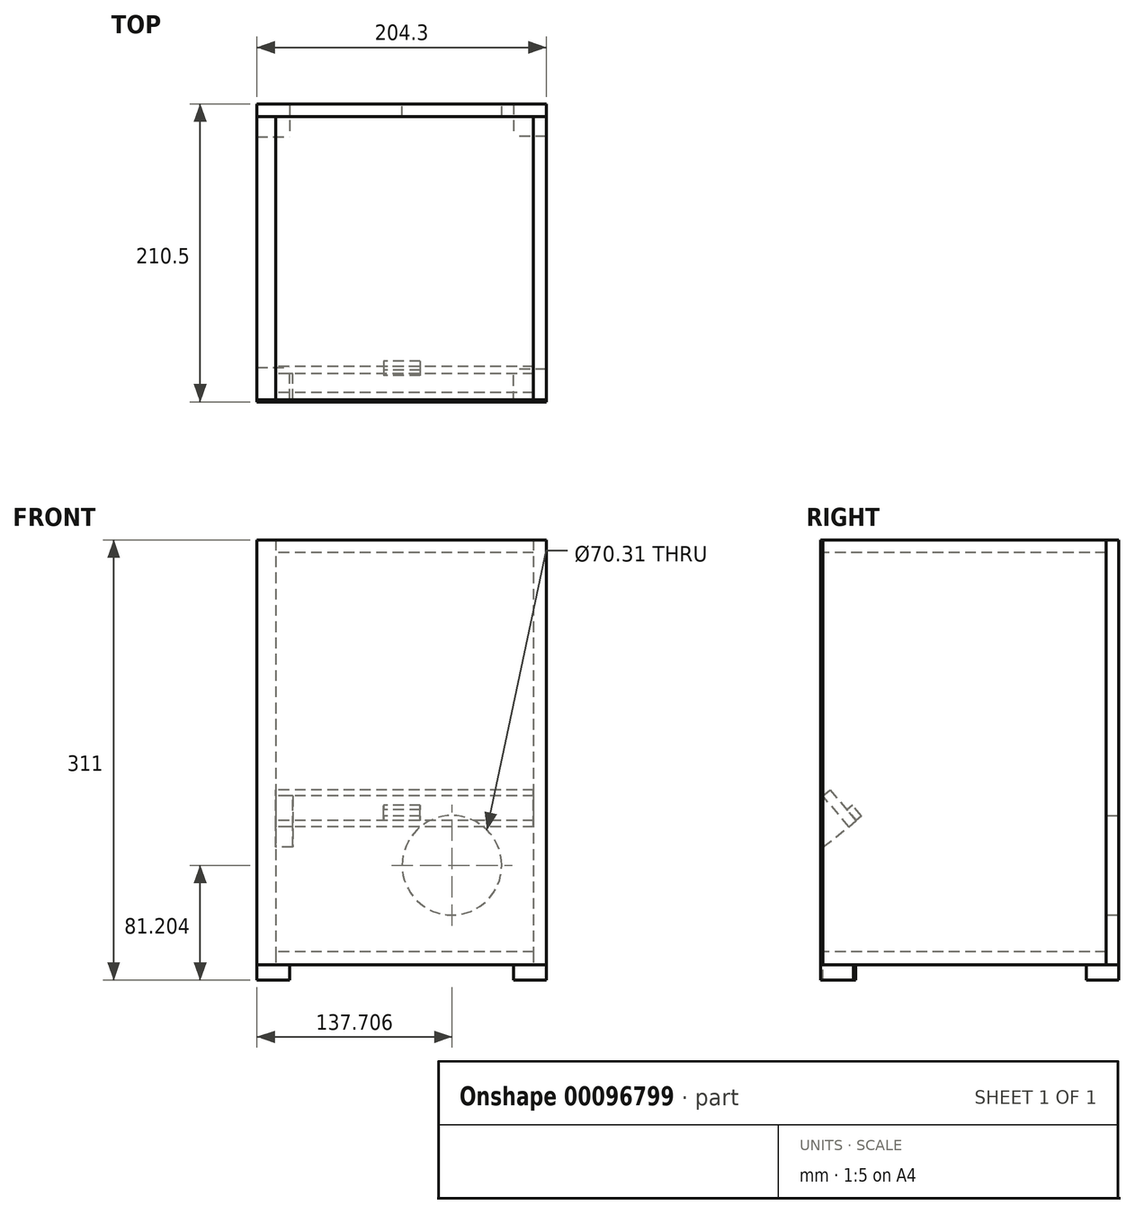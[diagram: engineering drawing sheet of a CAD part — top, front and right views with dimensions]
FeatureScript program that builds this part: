
annotation { "Feature Type Name" : "Feature", "Feature Type Description" : "" }
export const myFeature = defineFeature(function(context is Context, id is Id, definition is map)
    precondition{}
    {
        {
            var Q0;
            Q0=qCreatedBy(makeId("Front.planeOp"),FACE);
            var sketch = newSketch(context, id + "F0", { "sketchPlane" : qUnion([Q0])});
            skLineSegment(sketch, "E0.bottom", {"start": v(0, 0) * mm, "end": v(204.3, 0) * mm});
            skLineSegment(sketch, "E0.top", {"start": v(0, 300) * mm, "end": v(204.3, 300) * mm});
            skLineSegment(sketch, "E0.left", {"start": v(0, 0) * mm, "end": v(0, 300) * mm});
            skLineSegment(sketch, "E0.right", {"start": v(204.3, 0) * mm, "end": v(204.3, 300) * mm});
            skSolve(sketch);
        }
        {
            var Q0;
            Q0=makeQuery(id+"F0.imprint","IMPRINT",FACE,{"disambiguationData":[TD([[makeQuery(id+"F0.imprint","IMPRINT",EDGE,{"derivedFrom":sQuery(id+"F0.wireOp",EDGE,"E0.bottom")}),1.0]])]});
            extrude(context, id + "F1", {"entities" : qUnion([Q0]), "depth" : 1.5 * mm});
        }
        {
            var Q0;
            Q0=makeQuery(id+"F1.opExtrude","CAP_FACE",FACE,{"disambiguationData":[OSD([sQuery(id+"F0.wireOp",EDGE,"E0.bottom"),sQuery(id+"F0.wireOp",EDGE,"E0.top"),sQuery(id+"F0.wireOp",EDGE,"E0.left"),sQuery(id+"F0.wireOp",EDGE,"E0.right")])],"isStart":true});
            var sketch = newSketch(context, id + "F2", { "sketchPlane" : qUnion([Q0])});
            skLineSegment(sketch, "E1.bottom", {"start": v(0, 300) * mm, "end": v(-13.3, 300) * mm});
            skLineSegment(sketch, "E1.top", {"start": v(0, 0) * mm, "end": v(-13.3, 0) * mm});
            skLineSegment(sketch, "E1.left", {"start": v(0, 300) * mm, "end": v(0, 0) * mm});
            skLineSegment(sketch, "E1.right", {"start": v(-13.3, 300) * mm, "end": v(-13.3, 0) * mm});
            skSolve(sketch);
        }
        {
            var Q0;
            Q0 = qSketchRegion(id + "F2", true);
            extrude(context, id + "F3", {"entities" : qUnion([Q0]), "depth" : 200 * mm});
        }
        {
            var Q0;
            Q0=makeQuery(id+"F3.opExtrude","SWEPT_FACE",FACE,{"disambiguationData":[OSD([sQuery(id+"F2.wireOp",EDGE,"E1.right")])]});
            var sketch = newSketch(context, id + "F4", { "sketchPlane" : qUnion([Q0])});
            skLineSegment(sketch, "E2", {"start": v(0, 119.22) * mm, "end": v(0, 83.05) * mm});
            skLineSegment(sketch, "E3", {"start": v(0, 83.05) * mm, "end": v(18.44, 97.43) * mm});
            skLineSegment(sketch, "E4", {"start": v(18.44, 97.43) * mm, "end": v(0, 119.22) * mm});
            skSolve(sketch);
        }
        {
            var Q0;
            Q0 = qSketchRegion(id + "F4", true);
            extrude(context, id + "F5", {"entities" : qUnion([Q0]), "depth" : 12 * mm});
        }
        {
            var Q0;
            Q0=makeQuery(id+"F3.opExtrude","SWEPT_FACE",FACE,{"disambiguationData":[OSD([sQuery(id+"F2.wireOp",EDGE,"E1.right")])]});
            var sketch = newSketch(context, id + "F6", { "sketchPlane" : qUnion([Q0])});
            skLineSegment(sketch, "E5", {"start": v(18.44, 97.43) * mm, "end": v(0, 119.22) * mm});
            skLineSegment(sketch, "E6", {"start": v(18.44, 97.43) * mm, "end": v(23.47, 101.68) * mm});
            skLineSegment(sketch, "E7", {"start": v(0, 119.22) * mm, "end": v(5.03, 123.48) * mm});
            skLineSegment(sketch, "E8", {"start": v(5.03, 123.48) * mm, "end": v(23.47, 101.68) * mm});
            skSolve(sketch);
        }
        {
            var Q0;
            Q0 = qSketchRegion(id + "F6", true);
            extrude(context, id + "F7", {"entities" : qUnion([Q0]), "depth" : 182 * mm});
        }
        {
            var Q0;
            Q0=makeQuery(id+"F7.opExtrude","SWEPT_FACE",FACE,{"disambiguationData":[OSD([sQuery(id+"F6.wireOp",EDGE,"E8")])]});
            var sketch = newSketch(context, id + "F8", { "sketchPlane" : qUnion([Q0])});
            skLineSegment(sketch, "E9.bottom", {"start": v(-115.2, 62.47) * mm, "end": v(-89.47, 62.47) * mm});
            skLineSegment(sketch, "E9.top", {"start": v(-115.2, 72.45) * mm, "end": v(-89.47, 72.45) * mm});
            skLineSegment(sketch, "E9.left", {"start": v(-115.2, 62.47) * mm, "end": v(-115.2, 72.45) * mm});
            skLineSegment(sketch, "E9.right", {"start": v(-89.47, 62.47) * mm, "end": v(-89.47, 72.45) * mm});
            skSolve(sketch);
        }
        {
            var Q0;
            Q0 = qSketchRegion(id + "F8", true);
            extrude(context, id + "F9", {"entities" : qUnion([Q0]), "depth" : 5 * mm});
        }
        {
            var Q0;
            Q0=makeQuery(id+"F3.opExtrude","SWEPT_FACE",FACE,{"disambiguationData":[OSD([sQuery(id+"F2.wireOp",EDGE,"E1.right")])]});
            var sketch = newSketch(context, id + "F10", { "sketchPlane" : qUnion([Q0])});
            skLineSegment(sketch, "E10.bottom", {"start": v(200, 300) * mm, "end": v(0, 300) * mm});
            skLineSegment(sketch, "E10.top", {"start": v(200, 291) * mm, "end": v(0, 291) * mm});
            skLineSegment(sketch, "E10.left", {"start": v(200, 300) * mm, "end": v(200, 291) * mm});
            skLineSegment(sketch, "E10.right", {"start": v(0, 300) * mm, "end": v(0, 291) * mm});
            skSolve(sketch);
        }
        {
            var Q0;
            Q0 = qSketchRegion(id + "F10", true);
            extrude(context, id + "F11", {"entities" : qUnion([Q0]), "depth" : 182 * mm});
        }
        {
            var Q0;
            Q0=makeQuery(id+"F3.opExtrude","SWEPT_FACE",FACE,{"disambiguationData":[OSD([sQuery(id+"F2.wireOp",EDGE,"E1.right")])]});
            var sketch = newSketch(context, id + "F12", { "sketchPlane" : qUnion([Q0])});
            skLineSegment(sketch, "E11.bottom", {"start": v(200, 0) * mm, "end": v(0, 0) * mm});
            skLineSegment(sketch, "E11.top", {"start": v(200, 9) * mm, "end": v(0, 9) * mm});
            skLineSegment(sketch, "E11.left", {"start": v(200, 0) * mm, "end": v(200, 9) * mm});
            skLineSegment(sketch, "E11.right", {"start": v(0, 0) * mm, "end": v(0, 9) * mm});
            skSolve(sketch);
        }
        {
            var Q0;
            Q0 = qSketchRegion(id + "F12", true);
            extrude(context, id + "F13", {"entities" : qUnion([Q0]), "depth" : 182 * mm});
        }
        {
            var Q0;
            Q0=makeQuery(id+"F11.opExtrude","CAP_FACE",FACE,{"disambiguationData":[OSD([sQuery(id+"F10.wireOp",EDGE,"E10.bottom"),sQuery(id+"F10.wireOp",EDGE,"E10.top"),sQuery(id+"F10.wireOp",EDGE,"E10.left"),sQuery(id+"F10.wireOp",EDGE,"E10.right")])],"isStart":false});
            var sketch = newSketch(context, id + "F14", { "sketchPlane" : qUnion([Q0])});
            skLineSegment(sketch, "E12.bottom", {"start": v(200, 300) * mm, "end": v(0, 300) * mm});
            skLineSegment(sketch, "E12.top", {"start": v(200, 0) * mm, "end": v(0, 0) * mm});
            skLineSegment(sketch, "E12.left", {"start": v(200, 300) * mm, "end": v(200, 0) * mm});
            skLineSegment(sketch, "E12.right", {"start": v(0, 300) * mm, "end": v(0, 0) * mm});
            skSolve(sketch);
        }
        {
            var Q0;
            Q0 = qSketchRegion(id + "F14", true);
            extrude(context, id + "F15", {"entities" : qUnion([Q0]), "depth" : 9 * mm});
        }
        {
            var Q0;
            Q0=makeQuery(id+"F15.opExtrude","SWEPT_FACE",FACE,{"disambiguationData":[OSD([sQuery(id+"F14.wireOp",EDGE,"E12.left")])]});
            var sketch = newSketch(context, id + "F16", { "sketchPlane" : qUnion([Q0])});
            skLineSegment(sketch, "E13.bottom", {"start": v(-204.3, 300) * mm, "end": v(0, 300) * mm});
            skLineSegment(sketch, "E13.top", {"start": v(-204.3, 0) * mm, "end": v(0, 0) * mm});
            skLineSegment(sketch, "E13.left", {"start": v(-204.3, 300) * mm, "end": v(-204.3, 0) * mm});
            skLineSegment(sketch, "E13.right", {"start": v(0, 300) * mm, "end": v(0, 0) * mm});
            skSolve(sketch);
        }
        {
            var Q0;
            Q0 = qSketchRegion(id + "F16", true);
            extrude(context, id + "F17", {"entities" : qUnion([Q0]), "depth" : 9 * mm});
        }
        {
            var Q0;
            Q0=makeQuery(id+"F17.opExtrude","CAP_FACE",FACE,{"disambiguationData":[OSD([sQuery(id+"F16.wireOp",EDGE,"E13.bottom"),sQuery(id+"F16.wireOp",EDGE,"E13.top"),sQuery(id+"F16.wireOp",EDGE,"E13.left"),sQuery(id+"F16.wireOp",EDGE,"E13.right")])],"isStart":false});
            var sketch = newSketch(context, id + "F18", { "sketchPlane" : qUnion([Q0])});
            skCircle(sketch, "E14", {"center": v(-137.7, 70.2) * mm, "radius": 35.15 * mm});
            skSolve(sketch);
        }
        {
            var Q0;
            Q0 = qSketchRegion(id + "F18", true);
            extrude(context, id + "F19", {"entities" : qUnion([Q0]), "operationType" : NewBodyOperationType.REMOVE, "oppositeDirection" : true, "depth" : 9 * mm});
        }
        {
            var Q0;
            Q0 = qSketchRegion(id + "F18", true);
            extrude(context, id + "F20", {"entities" : qUnion([Q0]), "operationType" : NewBodyOperationType.REMOVE, "oppositeDirection" : true, "depth" : 25 * mm});
        }
        {
            var Q0;
            Q0=makeQuery(id+"F13.opExtrude","SWEPT_FACE",FACE,{"disambiguationData":[OSD([sQuery(id+"F12.wireOp",EDGE,"E11.bottom")])]});
            var sketch = newSketch(context, id + "F21", { "sketchPlane" : qUnion([Q0])});
            skLineSegment(sketch, "E15.bottom", {"start": v(204.3, -209) * mm, "end": v(181.3, -209) * mm});
            skLineSegment(sketch, "E15.top", {"start": v(204.3, -186) * mm, "end": v(181.3, -186) * mm});
            skLineSegment(sketch, "E15.left", {"start": v(204.3, -209) * mm, "end": v(204.3, -186) * mm});
            skLineSegment(sketch, "E15.right", {"start": v(181.3, -209) * mm, "end": v(181.3, -186) * mm});
            skSolve(sketch);
        }
        {
            var Q0;
            Q0 = qSketchRegion(id + "F21", true);
            extrude(context, id + "F22", {"entities" : qUnion([Q0]), "depth" : 11 * mm});
        }
        {
            var Q0;
            Q0=makeQuery(id+"F13.opExtrude","SWEPT_FACE",FACE,{"disambiguationData":[OSD([sQuery(id+"F12.wireOp",EDGE,"E11.bottom")])]});
            var sketch = newSketch(context, id + "F23", { "sketchPlane" : qUnion([Q0])});
            skLineSegment(sketch, "E16.bottom", {"start": v(0, -208.9) * mm, "end": v(23, -208.9) * mm});
            skLineSegment(sketch, "E16.top", {"start": v(0, -185.9) * mm, "end": v(23, -185.9) * mm});
            skLineSegment(sketch, "E16.left", {"start": v(0, -208.9) * mm, "end": v(0, -185.9) * mm});
            skLineSegment(sketch, "E16.right", {"start": v(23, -208.9) * mm, "end": v(23, -185.9) * mm});
            skSolve(sketch);
        }
        {
            var Q0;
            Q0 = qSketchRegion(id + "F23", true);
            extrude(context, id + "F24", {"entities" : qUnion([Q0]), "depth" : 11 * mm});
        }
        {
            var Q0;
            Q0=makeQuery(id+"F13.opExtrude","SWEPT_FACE",FACE,{"disambiguationData":[OSD([sQuery(id+"F12.wireOp",EDGE,"E11.bottom")])]});
            var sketch = newSketch(context, id + "F25", { "sketchPlane" : qUnion([Q0])});
            skLineSegment(sketch, "E17.bottom", {"start": v(0, 0) * mm, "end": v(23, 0) * mm});
            skLineSegment(sketch, "E17.top", {"start": v(0, -23) * mm, "end": v(23, -23) * mm});
            skLineSegment(sketch, "E17.left", {"start": v(0, 0) * mm, "end": v(0, -23) * mm});
            skLineSegment(sketch, "E17.right", {"start": v(23, 0) * mm, "end": v(23, -23) * mm});
            skSolve(sketch);
        }
        {
            var Q0;
            Q0 = qSketchRegion(id + "F25", true);
            extrude(context, id + "F26", {"entities" : qUnion([Q0]), "depth" : 11 * mm});
        }
        {
            var Q0;
            Q0=makeQuery(id+"F1.opExtrude","SWEPT_FACE",FACE,{"disambiguationData":[OSD([sQuery(id+"F0.wireOp",EDGE,"E0.bottom")])]});
            var sketch = newSketch(context, id + "F27", { "sketchPlane" : qUnion([Q0])});
            skLineSegment(sketch, "E18.bottom", {"start": v(204.3, 1.5) * mm, "end": v(181.3, 1.5) * mm});
            skLineSegment(sketch, "E18.top", {"start": v(204.3, -21.5) * mm, "end": v(181.3, -21.5) * mm});
            skLineSegment(sketch, "E18.left", {"start": v(204.3, 1.5) * mm, "end": v(204.3, -21.5) * mm});
            skLineSegment(sketch, "E18.right", {"start": v(181.3, 1.5) * mm, "end": v(181.3, -21.5) * mm});
            skSolve(sketch);
        }
        {
            var Q0;
            Q0 = qSketchRegion(id + "F27", true);
            extrude(context, id + "F28", {"entities" : qUnion([Q0]), "depth" : 11 * mm});
        }
    });
